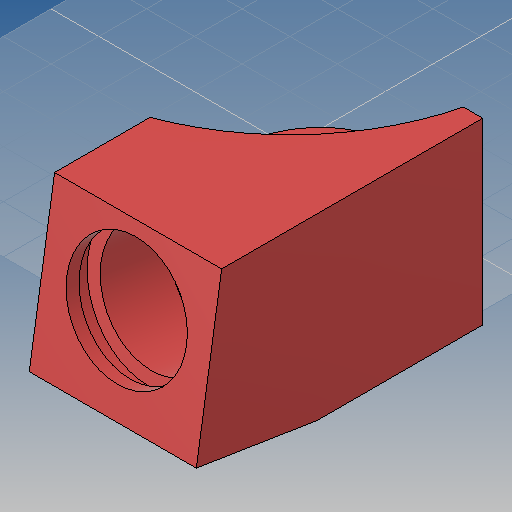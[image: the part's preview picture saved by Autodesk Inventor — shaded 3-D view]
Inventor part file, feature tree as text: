
AUTODESK INVENTOR PART (.ipt)
format: ipt  version: 2019 (Build 230136000, 136)  size: 224,768 bytes
history: native  units: mm
features: extrude x8, sketch x5, plane x3, other x2, projected_geometry x1
ambient origin geometry x8: Origin, YZ Plane, XZ Plane, XY Plane, X Axis, Y Axis, Z Axis, Center Point
bodies: Volumenkörper1 (feature_tree)
feature tree (19):
  other  "<userpath>\OneDrive\Dokumente\Inventor\Absauganlage\Absauganlage_Params.xlsx"
  sketch  "Skizze1"  dims[d0=200.0mm d1=4.9mm]
  extrude  "Extrusion1"  Depth=4.9mm
  plane  "Arbeitsebene1"
  sketch  "Skizze2"  dims[d2=46.2mm d3=50.0mm]
  extrude  "Extrusion4"  Depth=50.0mm
  plane  "Arbeitsebene4"
  sketch  "Skizze4"  dims[d6=55.0mm d7=75.0mm d8=0.0mm]
  extrude  "Extrusion8"  Depth=75.0mm TaperAngle=0.0deg
  extrude  "Extrusion9"  Depth=50.2mm
  extrude  "Extrusion10"  Depth=9.0mm
  extrude  "Extrusion11"  Depth=75.0mm TaperAngle=0.0deg
  extrude  "Extrusion12"  Depth=9.0mm
  plane  "Arbeitsebene6"
  extrude  "Extrusion13"  Depth=9.0mm
  projected_geometry  "Projizierte Kontur2"
  sketch  "Skizze6"  dims[d9=17.27876mm d10=50.2mm]
  sketch  "Skizze7"  dims[d11=37.5mm d12=2.0mm d17=75.0mm d18=0.0mm d27=73.0mm d28=8.552113mm d29=75.0mm d30=0.0mm d31=75.0mm d32=0.0mm d33=75.0mm d34=0.0mm d35=6.0mm d36=66.0mm d37=106.0mm d38=0.0mm d39=10.0mm d40=120.0mm d42=105.0mm d43=0.0mm d44=1.570796mm d45=1.570796mm d46=-10.0mm d47=61.0mm d48=9.0mm d49=0.0mm]
  other  "Schnittkanten projizieren1"
